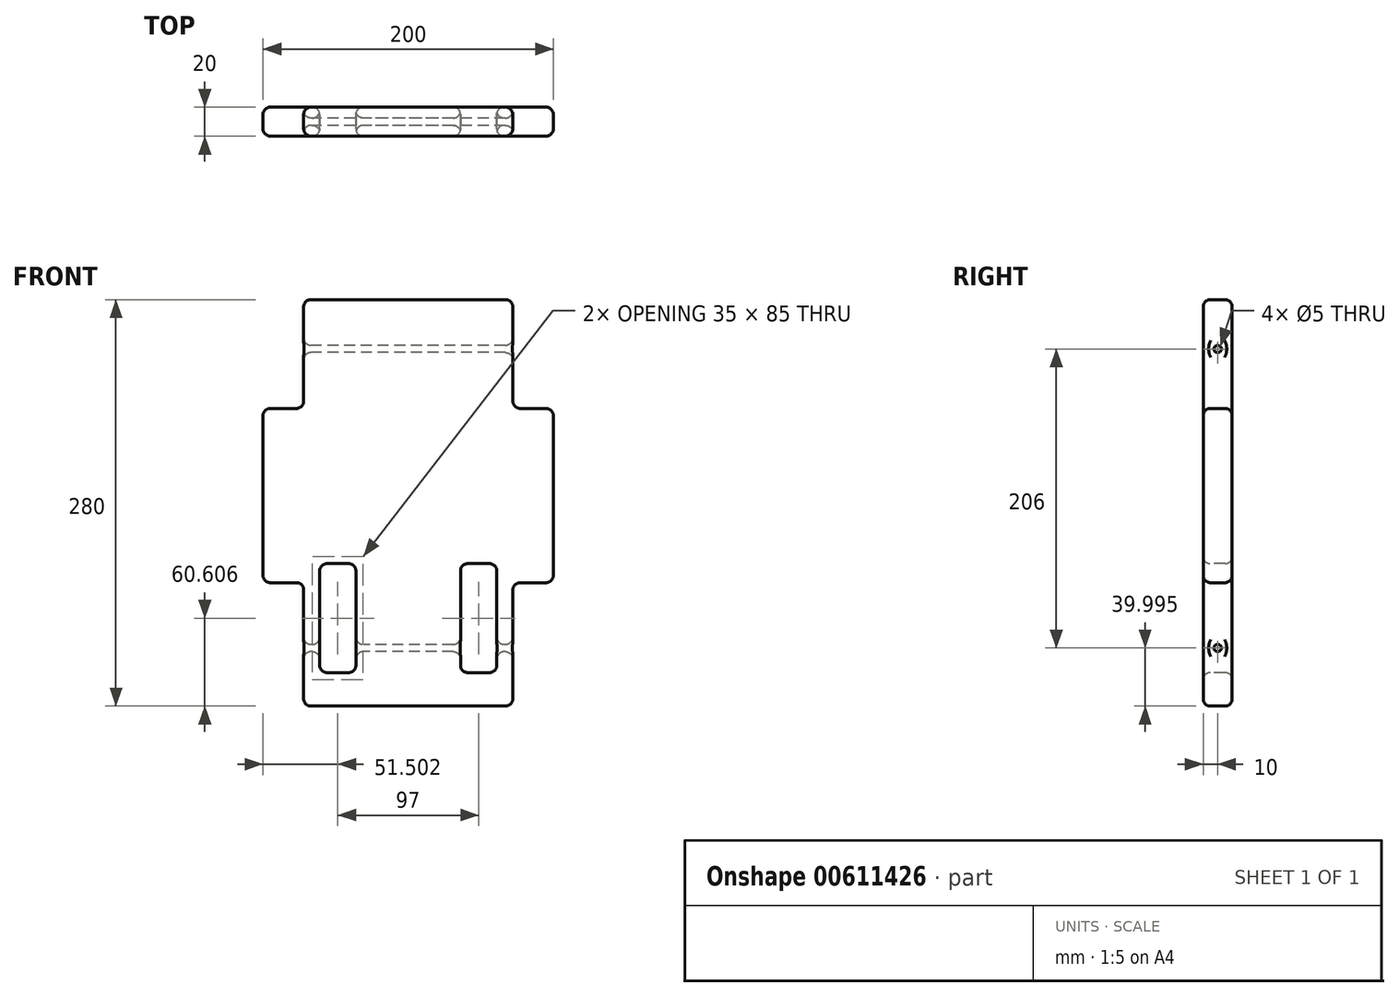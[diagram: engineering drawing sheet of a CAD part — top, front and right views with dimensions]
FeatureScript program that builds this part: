
annotation { "Feature Type Name" : "Feature", "Feature Type Description" : "" }
export const myFeature = defineFeature(function(context is Context, id is Id, definition is map)
    precondition{}
    {
        {
            var Q0;
            Q0=qCreatedBy(makeId("Front.planeOp"),FACE);
            var sketch = newSketch(context, id + "F0", { "sketchPlane" : qUnion([Q0])});
            skLineSegment(sketch, "E0.bottom", {"start": v(-101.4, -179.9) * mm, "end": v(98.6, -179.9) * mm});
            skLineSegment(sketch, "E0.top", {"start": v(-101.4, -459.9) * mm, "end": v(98.6, -459.9) * mm});
            skLineSegment(sketch, "E0.left", {"start": v(-101.4, -179.9) * mm, "end": v(-101.4, -459.9) * mm});
            skLineSegment(sketch, "E0.right", {"start": v(98.6, -179.9) * mm, "end": v(98.6, -459.9) * mm});
            skSolve(sketch);
        }
        {
            var Q0;
            Q0=makeQuery(id+"F0.imprint","IMPRINT",FACE,{"disambiguationData":[TD([[makeQuery(id+"F0.imprint","IMPRINT",EDGE,{"derivedFrom":sQuery(id+"F0.wireOp",EDGE,"E0.bottom")}),-1.0]])]});
            extrude(context, id + "F1", {"entities" : qUnion([Q0]), "depth" : 20 * mm, "offsetDistance" : 25.4 * mm});
        }
        {
            var Q0;
            Q0=makeQuery(id+"F1.opExtrude","CAP_FACE",FACE,{"disambiguationData":[OSD([sQuery(id+"F0.wireOp",EDGE,"E0.bottom"),sQuery(id+"F0.wireOp",EDGE,"E0.top"),sQuery(id+"F0.wireOp",EDGE,"E0.left"),sQuery(id+"F0.wireOp",EDGE,"E0.right")])],"isStart":false});
            var sketch = newSketch(context, id + "F2", { "sketchPlane" : qUnion([Q0])});
            skLineSegment(sketch, "E1.0", {"start": v(-73.4, -179.9) * mm, "end": v(-73.4, -459.9) * mm});
            skLineSegment(sketch, "E2.0", {"start": v(70.6, -179.9) * mm, "end": v(70.6, -459.9) * mm});
            skLineSegment(sketch, "E3.0", {"start": v(-101.4, -254.9) * mm, "end": v(98.6, -254.9) * mm});
            skLineSegment(sketch, "E4.0", {"start": v(-101.4, -374.9) * mm, "end": v(98.6, -374.9) * mm});
            skSolve(sketch);
        }
        {
            var Q0;
            {var subQ0=sQuery(id+"F2.wireOp",EDGE,"E1.0");var subQ1=makeQuery(id+"F1.opExtrude","CAP_EDGE",EDGE,{"disambiguationData":[OSD([sQuery(id+"F0.wireOp",EDGE,"E0.bottom")])],"isStart":false});var subQ2=makeQuery(id+"F2.imprint","INTERSECT",VERTEX,{"derivedFrom":[subQ1,subQ0]});Q0=makeQuery(id+"F2.imprint","IMPRINT",FACE,{"disambiguationData":[TD([[makeQuery(id+"F2.imprint","IMPRINT",EDGE,{"disambiguationData":[TD([[subQ2,-1.0]])],"derivedFrom":subQ0}),-1.0]])]});}
            extrude(context, id + "F3", {"entities" : qUnion([Q0]), "operationType" : NewBodyOperationType.REMOVE, "oppositeDirection" : true, "depth" : 25.4 * mm, "offsetDistance" : 25.4 * mm});
        }
        {
            var Q0;
            {var subQ0=sQuery(id+"F2.wireOp",EDGE,"E2.0");var subQ1=makeQuery(id+"F1.opExtrude","CAP_EDGE",EDGE,{"disambiguationData":[OSD([sQuery(id+"F0.wireOp",EDGE,"E0.bottom")])],"isStart":false});var subQ2=makeQuery(id+"F2.imprint","INTERSECT",VERTEX,{"derivedFrom":[subQ1,subQ0]});Q0=makeQuery(id+"F2.imprint","IMPRINT",FACE,{"disambiguationData":[TD([[makeQuery(id+"F2.imprint","IMPRINT",EDGE,{"disambiguationData":[TD([[subQ2,-1.0]])],"derivedFrom":subQ0}),1.0]])]});}
            extrude(context, id + "F4", {"entities" : qUnion([Q0]), "operationType" : NewBodyOperationType.REMOVE, "oppositeDirection" : true, "depth" : 25.4 * mm, "offsetDistance" : 25.4 * mm});
        }
        {
            var Q0;
            {var subQ0=sQuery(id+"F2.wireOp",EDGE,"E1.0");var subQ1=makeQuery(id+"F1.opExtrude","CAP_EDGE",EDGE,{"disambiguationData":[OSD([sQuery(id+"F0.wireOp",EDGE,"E0.top")])],"isStart":false});var subQ2=makeQuery(id+"F2.imprint","INTERSECT",VERTEX,{"derivedFrom":[subQ1,subQ0]});Q0=makeQuery(id+"F2.imprint","IMPRINT",FACE,{"disambiguationData":[TD([[makeQuery(id+"F2.imprint","IMPRINT",EDGE,{"disambiguationData":[TD([[subQ2,1.0]])],"derivedFrom":subQ0}),-1.0]])]});}
            extrude(context, id + "F5", {"entities" : qUnion([Q0]), "operationType" : NewBodyOperationType.REMOVE, "oppositeDirection" : true, "depth" : 25.4 * mm, "offsetDistance" : 25.4 * mm});
        }
        {
            var Q0;
            {var subQ0=sQuery(id+"F2.wireOp",EDGE,"E2.0");var subQ1=makeQuery(id+"F1.opExtrude","CAP_EDGE",EDGE,{"disambiguationData":[OSD([sQuery(id+"F0.wireOp",EDGE,"E0.top")])],"isStart":false});var subQ2=makeQuery(id+"F2.imprint","INTERSECT",VERTEX,{"derivedFrom":[subQ1,subQ0]});Q0=makeQuery(id+"F2.imprint","IMPRINT",FACE,{"disambiguationData":[TD([[makeQuery(id+"F2.imprint","IMPRINT",EDGE,{"disambiguationData":[TD([[subQ2,1.0]])],"derivedFrom":subQ0}),1.0]])]});}
            extrude(context, id + "F6", {"entities" : qUnion([Q0]), "operationType" : NewBodyOperationType.REMOVE, "oppositeDirection" : true, "depth" : 25.4 * mm, "offsetDistance" : 25.4 * mm});
        }
        {
            var Q0;
            {var subQ0=sQuery(id+"F2.wireOp",EDGE,"E1.0");var subQ1=makeQuery(id+"F1.opExtrude","CAP_EDGE",EDGE,{"disambiguationData":[OSD([sQuery(id+"F0.wireOp",EDGE,"E0.top")])],"isStart":false});var subQ2=makeQuery(id+"F2.imprint","INTERSECT",VERTEX,{"derivedFrom":[subQ1,subQ0]});Q0=makeQuery(id+"F2.imprint","IMPRINT",FACE,{"disambiguationData":[TD([[makeQuery(id+"F2.imprint","IMPRINT",EDGE,{"disambiguationData":[TD([[subQ2,1.0]])],"derivedFrom":subQ0}),1.0]])]});}
            var sketch = newSketch(context, id + "F7", { "sketchPlane" : qUnion([Q0])});
            skLineSegment(sketch, "E5.bottom", {"start": v(34.6, -361.8) * mm, "end": v(59.6, -361.8) * mm});
            skLineSegment(sketch, "E5.top", {"start": v(34.6, -436.8) * mm, "end": v(59.6, -436.8) * mm});
            skLineSegment(sketch, "E5.left", {"start": v(34.6, -361.8) * mm, "end": v(34.6, -436.8) * mm});
            skLineSegment(sketch, "E5.right", {"start": v(59.6, -361.8) * mm, "end": v(59.6, -436.8) * mm});
            skLineSegment(sketch, "E6.bottom", {"start": v(-62.4, -361.8) * mm, "end": v(-37.4, -361.8) * mm});
            skLineSegment(sketch, "E6.top", {"start": v(-62.4, -436.8) * mm, "end": v(-37.4, -436.8) * mm});
            skLineSegment(sketch, "E6.left", {"start": v(-62.4, -361.8) * mm, "end": v(-62.4, -436.8) * mm});
            skLineSegment(sketch, "E6.right", {"start": v(-37.4, -361.8) * mm, "end": v(-37.4, -436.8) * mm});
            skSolve(sketch);
        }
        {
            var Q0;
            {var subQ0=sQuery(id+"F7.wireOp",EDGE,"E6.top");Q0=makeQuery(id+"F7.imprint","IMPRINT",FACE,{"disambiguationData":[TD([[makeQuery(id+"F7.imprint","IMPRINT",EDGE,{"derivedFrom":subQ0}),1.0]])]});}
            var Q1;
            {var subQ0=sQuery(id+"F7.wireOp",EDGE,"E5.top");Q1=makeQuery(id+"F7.imprint","IMPRINT",FACE,{"disambiguationData":[TD([[makeQuery(id+"F7.imprint","IMPRINT",EDGE,{"derivedFrom":subQ0}),1.0]])]});}
            var Q2;
            {var subQ0=sQuery(id+"F7.wireOp",EDGE,"E6.bottom");Q2=makeQuery(id+"F7.imprint","IMPRINT",FACE,{"disambiguationData":[TD([[makeQuery(id+"F7.imprint","IMPRINT",EDGE,{"derivedFrom":subQ0}),-1.0]])]});}
            var Q3;
            {var subQ0=sQuery(id+"F7.wireOp",EDGE,"E5.bottom");Q3=makeQuery(id+"F7.imprint","IMPRINT",FACE,{"disambiguationData":[TD([[makeQuery(id+"F7.imprint","IMPRINT",EDGE,{"derivedFrom":subQ0}),-1.0]])]});}
            extrude(context, id + "F8", {"entities" : qUnion([Q0, Q1, Q2, Q3]), "operationType" : NewBodyOperationType.REMOVE, "oppositeDirection" : true, "depth" : 20 * mm, "offsetDistance" : 25.4 * mm});
        }
        {
            var Q0;
            Q0=makeQuery(id+"F3.boolean.opBoolean","COPY",FACE,{"derivedFrom":makeQuery(id+"F3.opExtrude","SWEPT_FACE",FACE,{"disambiguationData":[OSD([sQuery(id+"F2.wireOp",EDGE,"E1.0")])]})});
            var sketch = newSketch(context, id + "F9", { "sketchPlane" : qUnion([Q0])});
            skCircle(sketch, "E7", {"center": v(10, -213.9) * mm, "radius": 2.5 * mm});
            skSolve(sketch);
        }
        {
            var Q0;
            Q0=makeQuery(id+"F9.imprint","IMPRINT",FACE,{"disambiguationData":[TD([[makeQuery(id+"F9.imprint","IMPRINT",EDGE,{"derivedFrom":sQuery(id+"F9.wireOp",EDGE,"E7")}),1.0]])]});
            extrude(context, id + "F10", {"entities" : qUnion([Q0]), "operationType" : NewBodyOperationType.REMOVE, "oppositeDirection" : true, "depth" : 635 * mm, "offsetDistance" : 25.4 * mm});
        }
        {
            var Q0;
            Q0=makeQuery(id+"F5.boolean.opBoolean","COPY",FACE,{"derivedFrom":makeQuery(id+"F5.opExtrude","SWEPT_FACE",FACE,{"disambiguationData":[OSD([sQuery(id+"F2.wireOp",EDGE,"E1.0")])]})});
            var sketch = newSketch(context, id + "F11", { "sketchPlane" : qUnion([Q0])});
            skCircle(sketch, "E8", {"center": v(10, -419.9) * mm, "radius": 2.5 * mm});
            skSolve(sketch);
        }
        {
            var Q0;
            Q0=makeQuery(id+"F11.imprint","IMPRINT",FACE,{"disambiguationData":[TD([[makeQuery(id+"F11.imprint","IMPRINT",EDGE,{"derivedFrom":sQuery(id+"F11.wireOp",EDGE,"E8")}),1.0]])]});
            extrude(context, id + "F12", {"entities" : qUnion([Q0]), "operationType" : NewBodyOperationType.REMOVE, "oppositeDirection" : true, "depth" : 635 * mm, "offsetDistance" : 25.4 * mm});
        }
        {
            var Q0;
            Q0=makeQuery(id+"F4.boolean.opBoolean","COPY",FACE,{"derivedFrom":makeQuery(id+"F4.opExtrude","SWEPT_FACE",FACE,{"disambiguationData":[OSD([sQuery(id+"F2.wireOp",EDGE,"E2.0")])]})});
            var Q1;
            Q1=makeQuery(id+"F4.boolean.opBoolean","COPY",FACE,{"derivedFrom":makeQuery(id+"F4.opExtrude","SWEPT_FACE",FACE,{"disambiguationData":[OSD([sQuery(id+"F2.wireOp",EDGE,"E3.0")])]})});
            fillet(context, id + "F13", {"entities" : qUnion([Q0, Q1]), "radius" : 5.08 * mm, "tangentPropagation" : true, "allowEdgeOverflow" : false});
        }
        {
            var Q0;
            Q0=makeQuery(id+"F3.boolean.opBoolean","COPY",FACE,{"derivedFrom":makeQuery(id+"F3.opExtrude","SWEPT_FACE",FACE,{"disambiguationData":[OSD([sQuery(id+"F2.wireOp",EDGE,"E1.0")])]})});
            var Q1;
            Q1=makeQuery(id+"F3.boolean.opBoolean","COPY",FACE,{"derivedFrom":makeQuery(id+"F3.opExtrude","SWEPT_FACE",FACE,{"disambiguationData":[OSD([sQuery(id+"F2.wireOp",EDGE,"E3.0")])]})});
            fillet(context, id + "F14", {"entities" : qUnion([Q0, Q1]), "radius" : 5.08 * mm, "tangentPropagation" : true, "allowEdgeOverflow" : false});
        }
        {
            var Q0;
            Q0=makeQuery(id+"F5.boolean.opBoolean","COPY",FACE,{"derivedFrom":makeQuery(id+"F5.opExtrude","SWEPT_FACE",FACE,{"disambiguationData":[OSD([sQuery(id+"F2.wireOp",EDGE,"E4.0")])]})});
            var Q1;
            Q1=makeQuery(id+"F5.boolean.opBoolean","COPY",FACE,{"derivedFrom":makeQuery(id+"F5.opExtrude","SWEPT_FACE",FACE,{"disambiguationData":[OSD([sQuery(id+"F2.wireOp",EDGE,"E1.0")])]})});
            fillet(context, id + "F15", {"entities" : qUnion([Q0, Q1]), "radius" : 5.08 * mm, "tangentPropagation" : true, "allowEdgeOverflow" : false});
        }
        {
            var Q0;
            Q0=makeQuery(id+"F6.boolean.opBoolean","COPY",FACE,{"derivedFrom":makeQuery(id+"F6.opExtrude","SWEPT_FACE",FACE,{"disambiguationData":[OSD([sQuery(id+"F2.wireOp",EDGE,"E4.0")])]})});
            var Q1;
            Q1=makeQuery(id+"F6.boolean.opBoolean","COPY",FACE,{"derivedFrom":makeQuery(id+"F6.opExtrude","SWEPT_FACE",FACE,{"disambiguationData":[OSD([sQuery(id+"F2.wireOp",EDGE,"E2.0")])]})});
            fillet(context, id + "F16", {"entities" : qUnion([Q0, Q1]), "radius" : 5.08 * mm, "tangentPropagation" : true, "allowEdgeOverflow" : false});
        }
        {
            var Q0;
            Q0=makeQuery(id+"F14.opFillet","BLEND_FACE",FACE,{"disambiguationData":[OSD([sQuery(id+"F0.wireOp",EDGE,"E0.left"),sQuery(id+"F2.wireOp",EDGE,"E3.0")])]});
            var Q1;
            Q1=makeQuery(id+"F1.opExtrude","SWEPT_FACE",FACE,{"disambiguationData":[OSD([sQuery(id+"F0.wireOp",EDGE,"E0.left")])]});
            fillet(context, id + "F17", {"entities" : qUnion([Q0, Q1]), "radius" : 5.08 * mm, "tangentPropagation" : true, "allowEdgeOverflow" : false});
        }
        {
            var Q0;
            Q0=makeQuery(id+"F14.opFillet","BLEND_FACE",FACE,{"disambiguationData":[OSD([sQuery(id+"F0.wireOp",EDGE,"E0.bottom"),sQuery(id+"F2.wireOp",EDGE,"E1.0")])]});
            var Q1;
            Q1=makeQuery(id+"F1.opExtrude","SWEPT_FACE",FACE,{"disambiguationData":[OSD([sQuery(id+"F0.wireOp",EDGE,"E0.bottom")])]});
            var Q2;
            Q2=makeQuery(id+"F13.opFillet","BLEND_FACE",FACE,{"disambiguationData":[OSD([sQuery(id+"F0.wireOp",EDGE,"E0.bottom"),sQuery(id+"F2.wireOp",EDGE,"E2.0")])]});
            fillet(context, id + "F18", {"entities" : qUnion([Q0, Q1, Q2]), "radius" : 5.08 * mm, "tangentPropagation" : true, "allowEdgeOverflow" : false});
        }
        {
            var Q0;
            Q0=makeQuery(id+"F13.opFillet","BLEND_FACE",FACE,{"disambiguationData":[OSD([sQuery(id+"F0.wireOp",EDGE,"E0.right"),sQuery(id+"F2.wireOp",EDGE,"E3.0")])]});
            var Q1;
            Q1=makeQuery(id+"F1.opExtrude","SWEPT_FACE",FACE,{"disambiguationData":[OSD([sQuery(id+"F0.wireOp",EDGE,"E0.right")])]});
            var Q2;
            Q2=makeQuery(id+"F16.opFillet","BLEND_FACE",FACE,{"disambiguationData":[OSD([sQuery(id+"F0.wireOp",EDGE,"E0.right"),sQuery(id+"F2.wireOp",EDGE,"E4.0")])]});
            fillet(context, id + "F19", {"entities" : qUnion([Q0, Q1, Q2]), "radius" : 5.08 * mm, "tangentPropagation" : true, "allowEdgeOverflow" : false});
        }
        {
            var Q0;
            Q0=makeQuery(id+"F15.opFillet","BLEND_FACE",FACE,{"disambiguationData":[OSD([sQuery(id+"F0.wireOp",EDGE,"E0.top"),sQuery(id+"F2.wireOp",EDGE,"E1.0")])]});
            var Q1;
            Q1=makeQuery(id+"F1.opExtrude","SWEPT_FACE",FACE,{"disambiguationData":[OSD([sQuery(id+"F0.wireOp",EDGE,"E0.top")])]});
            var Q2;
            Q2=makeQuery(id+"F16.opFillet","BLEND_FACE",FACE,{"disambiguationData":[OSD([sQuery(id+"F0.wireOp",EDGE,"E0.top"),sQuery(id+"F2.wireOp",EDGE,"E2.0")])]});
            fillet(context, id + "F20", {"entities" : qUnion([Q0, Q1, Q2]), "radius" : 5.08 * mm, "tangentPropagation" : true, "allowEdgeOverflow" : false});
        }
        {
            var Q0;
            Q0=makeQuery(id+"F8.boolean.opBoolean","COPY",FACE,{"derivedFrom":makeQuery(id+"F8.opExtrude","SWEPT_FACE",FACE,{"disambiguationData":[OSD([sQuery(id+"F7.wireOp",EDGE,"E5.left")])]})});
            var Q1;
            Q1=makeQuery(id+"F8.boolean.opBoolean","COPY",FACE,{"derivedFrom":makeQuery(id+"F8.opExtrude","SWEPT_FACE",FACE,{"disambiguationData":[OSD([sQuery(id+"F7.wireOp",EDGE,"E5.right")])]})});
            var Q2;
            Q2=makeQuery(id+"F8.boolean.opBoolean","COPY",FACE,{"derivedFrom":makeQuery(id+"F8.opExtrude","SWEPT_FACE",FACE,{"disambiguationData":[OSD([sQuery(id+"F7.wireOp",EDGE,"E5.bottom")])]})});
            var Q3;
            Q3=makeQuery(id+"F8.boolean.opBoolean","COPY",FACE,{"derivedFrom":makeQuery(id+"F8.opExtrude","SWEPT_FACE",FACE,{"disambiguationData":[OSD([sQuery(id+"F7.wireOp",EDGE,"E6.bottom")])]})});
            var Q4;
            Q4=makeQuery(id+"F8.boolean.opBoolean","COPY",FACE,{"derivedFrom":makeQuery(id+"F8.opExtrude","SWEPT_FACE",FACE,{"disambiguationData":[OSD([sQuery(id+"F7.wireOp",EDGE,"E6.right")])]})});
            var Q5;
            Q5=makeQuery(id+"F8.boolean.opBoolean","COPY",FACE,{"derivedFrom":makeQuery(id+"F8.opExtrude","SWEPT_FACE",FACE,{"disambiguationData":[OSD([sQuery(id+"F7.wireOp",EDGE,"E5.top")])]})});
            var Q6;
            Q6=makeQuery(id+"F8.boolean.opBoolean","COPY",FACE,{"derivedFrom":makeQuery(id+"F8.opExtrude","SWEPT_FACE",FACE,{"disambiguationData":[OSD([sQuery(id+"F7.wireOp",EDGE,"E6.left")])]})});
            var Q7;
            Q7=makeQuery(id+"F8.boolean.opBoolean","COPY",FACE,{"derivedFrom":makeQuery(id+"F8.opExtrude","SWEPT_FACE",FACE,{"disambiguationData":[OSD([sQuery(id+"F7.wireOp",EDGE,"E6.top")])]})});
            fillet(context, id + "F21", {"entities" : qUnion([Q0, Q1, Q2, Q3, Q4, Q5, Q6, Q7]), "radius" : 5 * mm, "tangentPropagation" : true, "allowEdgeOverflow" : false});
        }
    });
